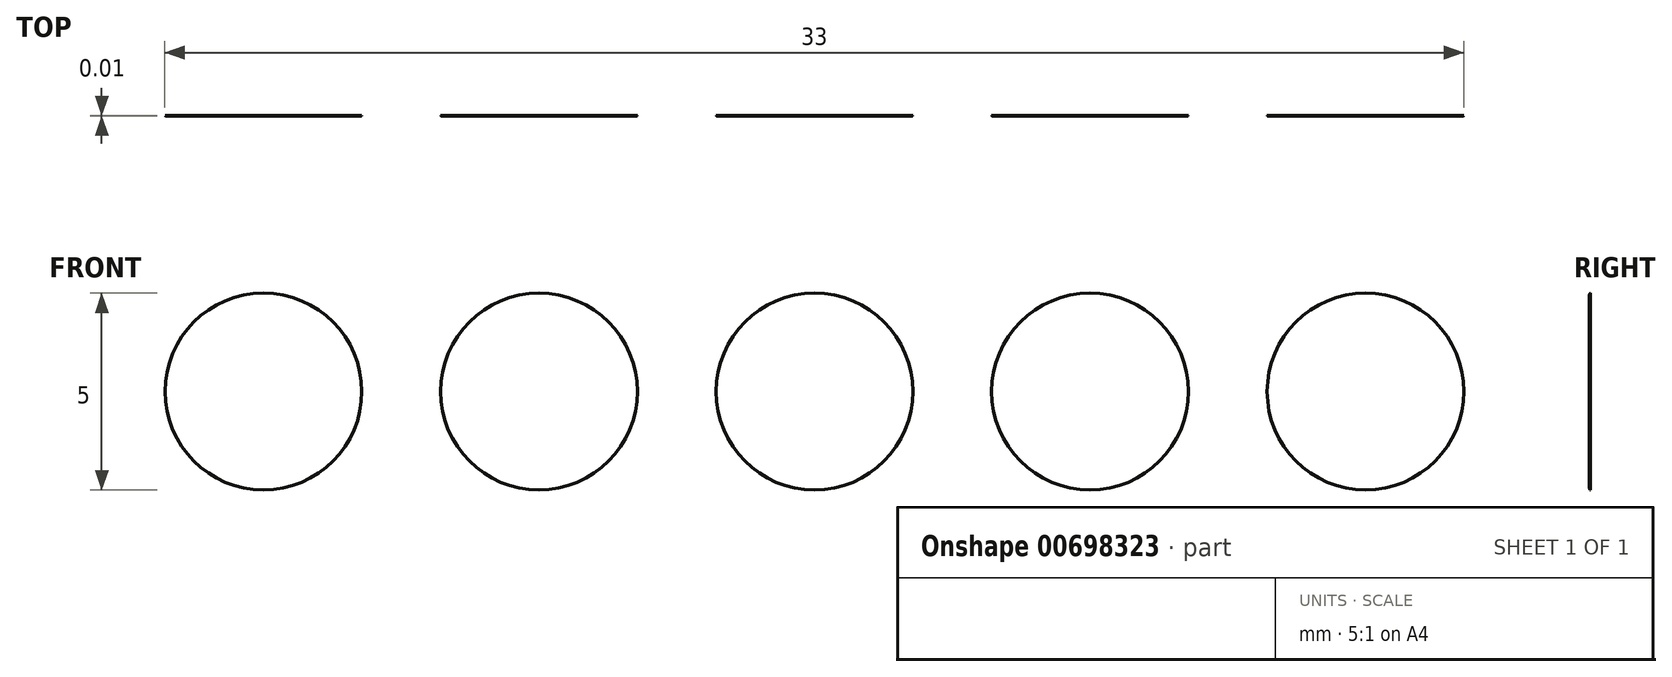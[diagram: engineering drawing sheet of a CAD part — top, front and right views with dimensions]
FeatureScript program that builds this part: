
annotation { "Feature Type Name" : "Feature", "Feature Type Description" : "" }
export const myFeature = defineFeature(function(context is Context, id is Id, definition is map)
    precondition{}
    {
        {
            var Q0;
            Q0=qCreatedBy(makeId("Front.planeOp"),FACE);
            var sketch = newSketch(context, id + "F0", { "sketchPlane" : qUnion([Q0])});
            skCircle(sketch, "E0", {"center": v(-6.75, 4.26) * mm, "radius": 2.5 * mm});
            skCircle(sketch, "E1", {"center": v(0.25, 4.26) * mm, "radius": 2.5 * mm});
            skCircle(sketch, "E2", {"center": v(7.25, 4.26) * mm, "radius": 2.5 * mm});
            skCircle(sketch, "E3", {"center": v(14.25, 4.26) * mm, "radius": 2.5 * mm});
            skCircle(sketch, "E4", {"center": v(21.25, 4.26) * mm, "radius": 2.5 * mm});
            skSolve(sketch);
        }
        {
            var Q0;
            Q0=makeQuery(id+"F0.imprint","IMPRINT",FACE,{"disambiguationData":[TD([[makeQuery(id+"F0.imprint","IMPRINT",EDGE,{"derivedFrom":sQuery(id+"F0.wireOp",EDGE,"E0")}),1.0]])]});
            var Q1;
            Q1=makeQuery(id+"F0.imprint","IMPRINT",FACE,{"disambiguationData":[TD([[makeQuery(id+"F0.imprint","IMPRINT",EDGE,{"derivedFrom":sQuery(id+"F0.wireOp",EDGE,"E1")}),1.0]])]});
            var Q2;
            Q2=makeQuery(id+"F0.imprint","IMPRINT",FACE,{"disambiguationData":[TD([[makeQuery(id+"F0.imprint","IMPRINT",EDGE,{"derivedFrom":sQuery(id+"F0.wireOp",EDGE,"E2")}),1.0]])]});
            var Q3;
            Q3=makeQuery(id+"F0.imprint","IMPRINT",FACE,{"disambiguationData":[TD([[makeQuery(id+"F0.imprint","IMPRINT",EDGE,{"derivedFrom":sQuery(id+"F0.wireOp",EDGE,"E3")}),1.0]])]});
            var Q4;
            Q4=makeQuery(id+"F0.imprint","IMPRINT",FACE,{"disambiguationData":[TD([[makeQuery(id+"F0.imprint","IMPRINT",EDGE,{"derivedFrom":sQuery(id+"F0.wireOp",EDGE,"E4")}),1.0]])]});
            extrude(context, id + "F1", {"entities" : qUnion([Q0, Q1, Q2, Q3, Q4]), "depth" : 6 / 406.4 * mm, "offsetDistance" : 25 * mm, "hasDraft" : true, "draftAngle" : 14 * degree, "draftPullDirection" : true});
        }
        {
            var Q0;
            Q0=makeQuery(id+"F1.opExtrude","CAP_EDGE",EDGE,{"disambiguationData":[OSD([sQuery(id+"F0.wireOp",EDGE,"E0")])],"isStart":false});
            var Q1;
            Q1=makeQuery(id+"F1.opExtrude","CAP_EDGE",EDGE,{"disambiguationData":[OSD([sQuery(id+"F0.wireOp",EDGE,"E1")])],"isStart":false});
            var Q2;
            Q2=makeQuery(id+"F1.opExtrude","CAP_EDGE",EDGE,{"disambiguationData":[OSD([sQuery(id+"F0.wireOp",EDGE,"E2")])],"isStart":false});
            var Q3;
            Q3=makeQuery(id+"F1.opExtrude","CAP_EDGE",EDGE,{"disambiguationData":[OSD([sQuery(id+"F0.wireOp",EDGE,"E3")])],"isStart":false});
            var Q4;
            Q4=makeQuery(id+"F1.opExtrude","CAP_EDGE",EDGE,{"disambiguationData":[OSD([sQuery(id+"F0.wireOp",EDGE,"E4")])],"isStart":false});
            fillet(context, id + "F2", {"entities" : qUnion([Q0, Q1, Q2, Q3, Q4]), "radius" : 0.1 * mm, "tangentPropagation" : true, "allowEdgeOverflow" : false});
        }
    });
